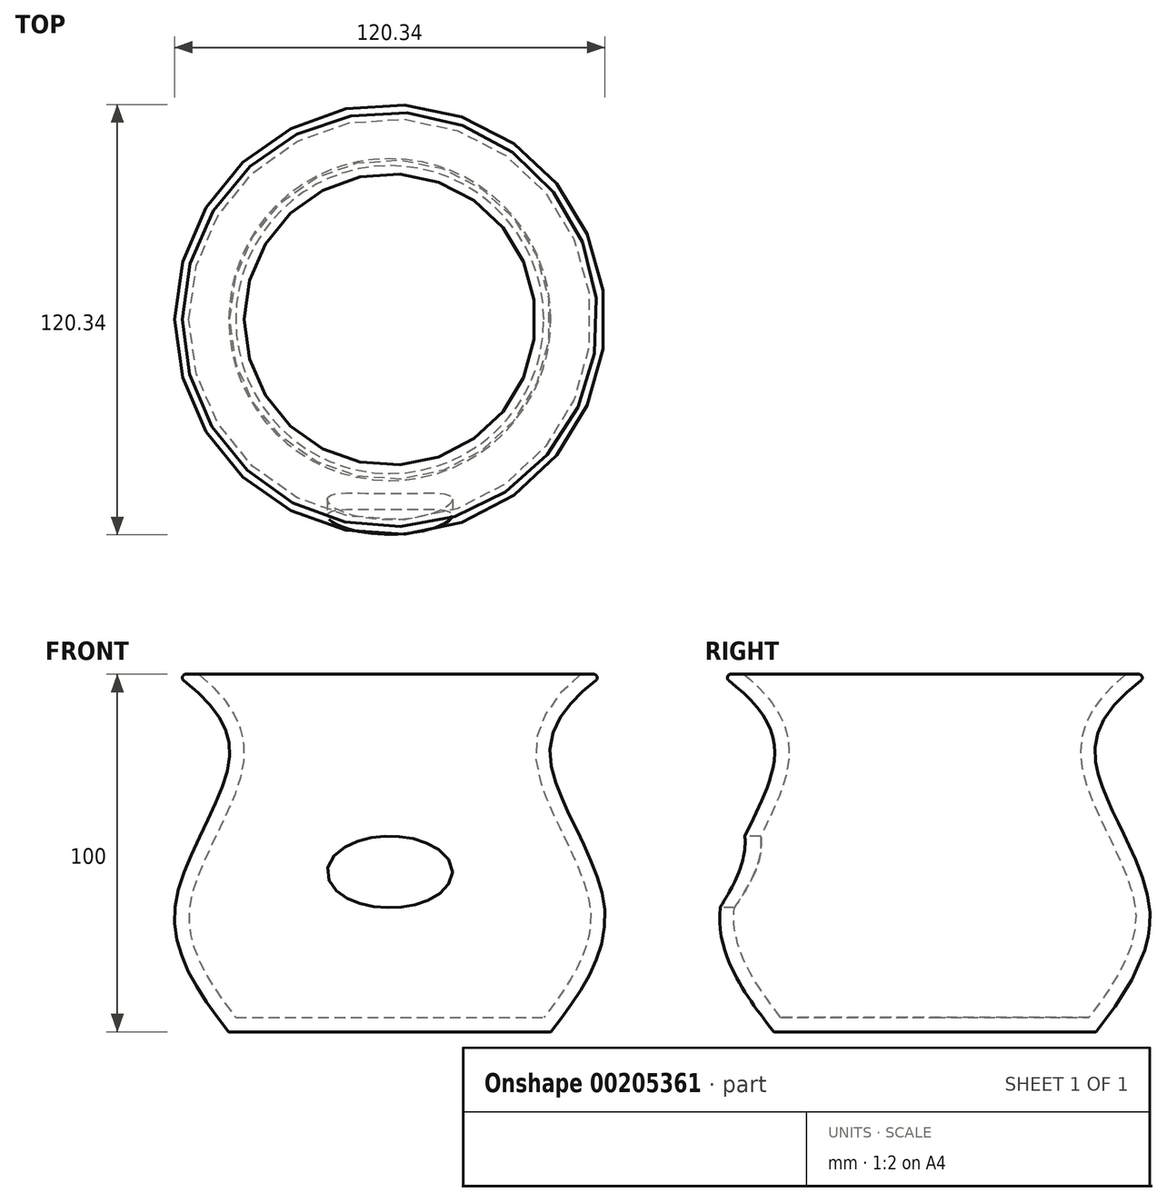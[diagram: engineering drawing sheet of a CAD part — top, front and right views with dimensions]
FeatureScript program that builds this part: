
annotation { "Feature Type Name" : "Feature", "Feature Type Description" : "" }
export const myFeature = defineFeature(function(context is Context, id is Id, definition is map)
    precondition{}
    {
        {
            var Q0;
            Q0=qCreatedBy(makeId("Front.planeOp"),FACE);
            var sketch = newSketch(context, id + "F0", { "sketchPlane" : qUnion([Q0])});
            skLineSegment(sketch, "E0.bottom", {"start": v(0, 0) * mm, "end": v(-45, 0) * mm});
            skLineSegment(sketch, "E0.top", {"start": v(0, 100) * mm, "end": v(-60, 100) * mm});
            skLineSegment(sketch, "E0.left", {"start": v(0, 0) * mm, "end": v(0, 100) * mm});
            skFitSpline(sketch, "E1", {"points": [v(-60, 100) * mm, v(-45, 75) * mm, v(-60, 35) * mm, v(-45, 0) * mm], "startDerivative": vector(114.08, -82.3) * mm, "endDerivative": vector(77.31, -98.02) * mm});
            skSolve(sketch);
        }
        {
            var Q0;
            Q0=makeQuery(id+"F0.imprint","IMPRINT",FACE,{"disambiguationData":[TD([[makeQuery(id+"F0.imprint","IMPRINT",EDGE,{"derivedFrom":sQuery(id+"F0.wireOp",EDGE,"E0.bottom")}),-1.0]])]});
            var Q1;
            Q1=sQuery(id+"F0.wireOp",EDGE,"E0.left");
            revolve(context, id + "F1", {"entities" : qUnion([Q0]), "axis" : qUnion([Q1]), "revolveType" : RevolveType.FULL});
        }
        {
            var Q0;
            Q0=makeQuery(id+"F1.opRevolve","SWEPT_FACE",FACE,{"disambiguationData":[OSD([sQuery(id+"F0.wireOp",EDGE,"E0.top")])]});
            shell(context, id + "F2", {"entities" : qUnion([Q0]), "thickness" : 4 * mm});
        }
        {
            var Q0;
            Q0=makeQuery(id+"F1.opRevolve","SWEPT_EDGE",EDGE,{"disambiguationData":[OSD([sQuery(id+"F0.wireOp",EDGE,"E0.top"),sQuery(id+"F0.wireOp",EDGE,"E1")])]});
            var Q1;
            Q1=makeQuery(id+"F2.opShell","OFFSET_EDGE",EDGE,{"disambiguationData":[OSD([sQuery(id+"F0.wireOp",EDGE,"E0.top"),sQuery(id+"F0.wireOp",EDGE,"E1")])]});
            fillet(context, id + "F3", {"entities" : qUnion([Q0, Q1]), "radius" : 1 * mm, "tangentPropagation" : true, "allowEdgeOverflow" : false});
        }
        {
            var Q0;
            Q0=qCreatedBy(makeId("Front.planeOp"),FACE);
            cPlane(context, id + "F4", {"entities" : qUnion([Q0]), "cplaneType" : CPlaneType.OFFSET, "offset" : 70 * mm, "width" : 150 * mm, "height" : 150 * mm});
        }
        {
            var Q0;
            Q0=qCreatedBy(id+"F4.planeOp",FACE);
            var sketch = newSketch(context, id + "F5", { "sketchPlane" : qUnion([Q0])});
            skEllipse(sketch, "E2", {"center": v(0, 44.7) * mm, "majorRadius": 17.5 * mm, "minorRadius": 10 * mm, "majorAxis": v(1, 0)});
            skSolve(sketch);
        }
        {
            var Q0;
            Q0 = qSketchRegion(id + "F5", true);
            extrude(context, id + "F6", {"entities" : qUnion([Q0]), "operationType" : NewBodyOperationType.REMOVE, "oppositeDirection" : true, "depth" : 30 * mm});
        }
    });
